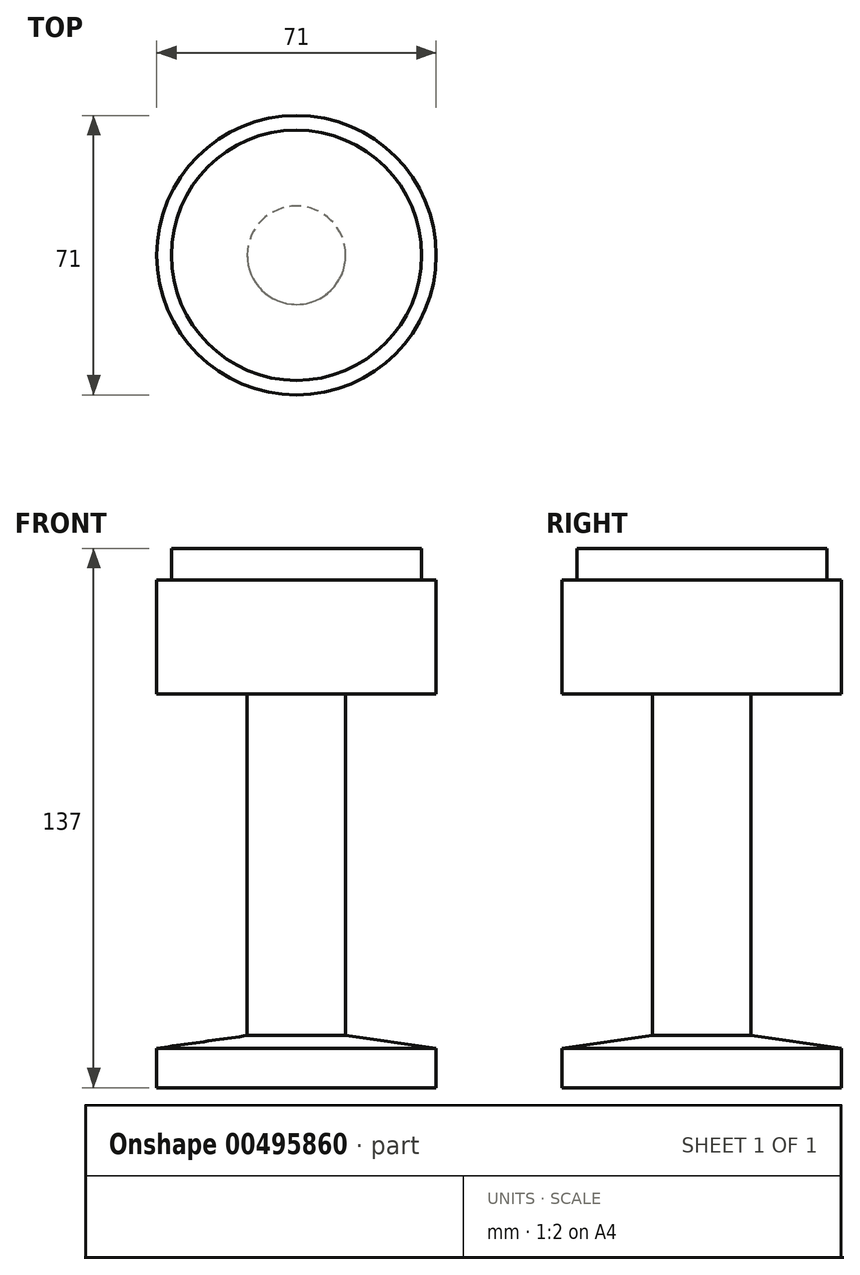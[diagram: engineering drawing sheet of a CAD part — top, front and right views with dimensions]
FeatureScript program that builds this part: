
annotation { "Feature Type Name" : "Feature", "Feature Type Description" : "" }
export const myFeature = defineFeature(function(context is Context, id is Id, definition is map)
    precondition{}
    {
        {
            var Q0;
            Q0=qCreatedBy(makeId("Right.planeOp"),FACE);
            var sketch = newSketch(context, id + "F0", { "sketchPlane" : qUnion([Q0])});
            skLineSegment(sketch, "E0", {"start": v(0, -49.8) * mm, "end": v(0, 54.76) * mm, "construction": true});
            skLineSegment(sketch, "E1", {"start": v(0, 15) * mm, "end": v(-35.5, 10) * mm});
            skLineSegment(sketch, "E2", {"start": v(-35.5, 10) * mm, "end": v(-35.5, 0) * mm});
            skLineSegment(sketch, "E3", {"start": v(-35.5, 0) * mm, "end": v(0, 0) * mm});
            skLineSegment(sketch, "E4", {"start": v(0, 0) * mm, "end": v(0, 15) * mm});
            skSolve(sketch);
        }
        {
            var Q0;
            Q0=qSketchRegion(id+"F0",true);
            var Q1;
            Q1=sQuery(id+"F0.wireOp",EDGE,"E0");
            revolve(context, id + "F1", {"entities" : qUnion([Q0]), "axis" : qUnion([Q1]), "revolveType" : RevolveType.FULL});
        }
        {
            var Q0;
            Q0=qCreatedBy(makeId("Top.planeOp"),FACE);
            var sketch = newSketch(context, id + "F2", { "sketchPlane" : qUnion([Q0])});
            skCircle(sketch, "E5", {"center": v(0, 0) * mm, "radius": 12.5 * mm});
            skSolve(sketch);
        }
        {
            var Q0;
            Q0=qSketchRegion(id+"F2",true);
            extrude(context, id + "F3", {"entities" : qUnion([Q0]), "operationType" : NewBodyOperationType.ADD, "depth" : 100 * mm});
        }
        {
            var Q0;
            Q0=makeQuery(id+"F3.opExtrude","CAP_FACE",FACE,{"disambiguationData":[OSD([sQuery(id+"F2.wireOp",EDGE,"E5")])],"isStart":false});
            var sketch = newSketch(context, id + "F4", { "sketchPlane" : qUnion([Q0])});
            skCircle(sketch, "E6.0", {"center": v(0, 0) * mm, "radius": 35.5 * mm});
            skSolve(sketch);
        }
        {
            var Q0;
            Q0=qSketchRegion(id+"F4",true);
            extrude(context, id + "F5", {"entities" : qUnion([Q0]), "operationType" : NewBodyOperationType.ADD, "depth" : 29 * mm});
        }
        {
            var Q0;
            Q0=makeQuery(id+"F5.opExtrude","CAP_FACE",FACE,{"disambiguationData":[OSD([sQuery(id+"F4.wireOp",EDGE,"E6.0")])],"isStart":false});
            var sketch = newSketch(context, id + "F6", { "sketchPlane" : qUnion([Q0])});
            skCircle(sketch, "E7", {"center": v(0, 0) * mm, "radius": 31.8 * mm});
            skSolve(sketch);
        }
        {
            var Q0;
            Q0=qSketchRegion(id+"F6",true);
            extrude(context, id + "F7", {"entities" : qUnion([Q0]), "operationType" : NewBodyOperationType.ADD, "depth" : 8 * mm});
        }
    });
